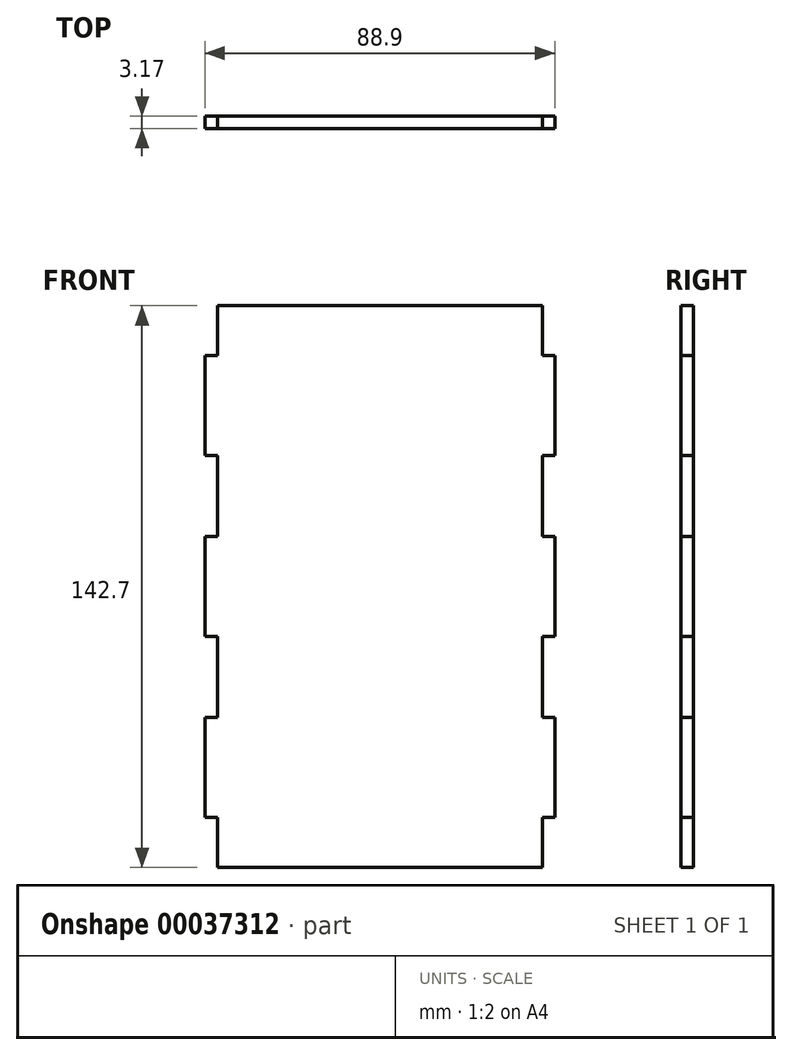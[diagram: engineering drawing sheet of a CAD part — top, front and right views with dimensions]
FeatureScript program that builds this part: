
annotation { "Feature Type Name" : "Feature", "Feature Type Description" : "" }
export const myFeature = defineFeature(function(context is Context, id is Id, definition is map)
    precondition{}
    {
        {
            var Q0;
            Q0=qCreatedBy(makeId("Front.planeOp"),FACE);
            var sketch = newSketch(context, id + "F0", { "sketchPlane" : qUnion([Q0])});
            skLineSegment(sketch, "E0.rect.bottom", {"start": v(44.45, -71.35) * mm, "end": v(-44.45, -71.35) * mm});
            skLineSegment(sketch, "E0.rect.top", {"start": v(44.45, 71.35) * mm, "end": v(-44.45, 71.35) * mm});
            skLineSegment(sketch, "E0.rect.left", {"start": v(44.45, -71.35) * mm, "end": v(44.45, 71.35) * mm});
            skLineSegment(sketch, "E0.rect.right", {"start": v(-44.45, -71.35) * mm, "end": v(-44.45, 71.35) * mm});
            skPoint(sketch, "E0.rect.middle", {"position": v(0, 0) * mm});
            skLineSegment(sketch, "E1", {"start": v(-44.45, 58.65) * mm, "end": v(-41.28, 58.65) * mm});
            skLineSegment(sketch, "E2", {"start": v(-44.45, 33.25) * mm, "end": v(-41.28, 33.25) * mm});
            skLineSegment(sketch, "E3", {"start": v(-41.28, 12.7) * mm, "end": v(-44.45, 12.7) * mm});
            skLineSegment(sketch, "E4", {"start": v(-44.45, -12.7) * mm, "end": v(-41.28, -12.7) * mm});
            skLineSegment(sketch, "E5", {"start": v(-41.28, -33.25) * mm, "end": v(-44.45, -33.25) * mm});
            skLineSegment(sketch, "E6", {"start": v(-44.45, -58.65) * mm, "end": v(-41.28, -58.65) * mm});
            skLineSegment(sketch, "E7", {"start": v(0, 71.35) * mm, "end": v(0, -71.35) * mm, "construction": true});
            skLineSegment(sketch, "E8", {"start": v(-41.28, 58.65) * mm, "end": v(-41.28, 71.35) * mm});
            skLineSegment(sketch, "E9", {"start": v(-41.28, 33.25) * mm, "end": v(-41.28, 12.7) * mm});
            skLineSegment(sketch, "E10", {"start": v(-41.28, -12.7) * mm, "end": v(-41.28, -33.25) * mm});
            skLineSegment(sketch, "E11", {"start": v(-41.28, -58.65) * mm, "end": v(-41.28, -71.35) * mm});
            skLineSegment(sketch, "E12.MirrorCS", {"start": v(41.28, 58.65) * mm, "end": v(41.28, 71.35) * mm});
            skLineSegment(sketch, "E13.MirrorCS", {"start": v(44.45, 58.65) * mm, "end": v(41.28, 58.65) * mm});
            skLineSegment(sketch, "E14.MirrorCS", {"start": v(-44.45, 71.35) * mm, "end": v(44.45, 71.35) * mm});
            skLineSegment(sketch, "E15.MirrorCS", {"start": v(41.28, 33.25) * mm, "end": v(41.28, 12.7) * mm});
            skLineSegment(sketch, "E16.MirrorCS", {"start": v(44.45, 33.25) * mm, "end": v(41.28, 33.25) * mm});
            skLineSegment(sketch, "E17.MirrorCS", {"start": v(41.28, 12.7) * mm, "end": v(44.45, 12.7) * mm});
            skLineSegment(sketch, "E18.MirrorCS", {"start": v(44.45, -12.7) * mm, "end": v(41.28, -12.7) * mm});
            skLineSegment(sketch, "E19.MirrorCS", {"start": v(41.28, -12.7) * mm, "end": v(41.28, -33.25) * mm});
            skLineSegment(sketch, "E20.MirrorCS", {"start": v(41.28, -33.25) * mm, "end": v(44.45, -33.25) * mm});
            skLineSegment(sketch, "E21.MirrorCS", {"start": v(44.45, -58.65) * mm, "end": v(41.28, -58.65) * mm});
            skLineSegment(sketch, "E22.MirrorCS", {"start": v(41.28, -58.65) * mm, "end": v(41.28, -71.35) * mm});
            skSolve(sketch);
        }
        {
            var Q0;
            {var subQ10=sQuery(id+"F0.wireOp",EDGE,"E1");Q0=makeQuery(id+"F0.imprint","IMPRINT",FACE,{"disambiguationData":[TD([[makeQuery(id+"F0.imprint","IMPRINT",EDGE,{"derivedFrom":subQ10}),-1.0]])]});}
            extrude(context, id + "F1", {"entities" : qUnion([Q0]), "depth" : 3.17 * mm});
        }
    });
